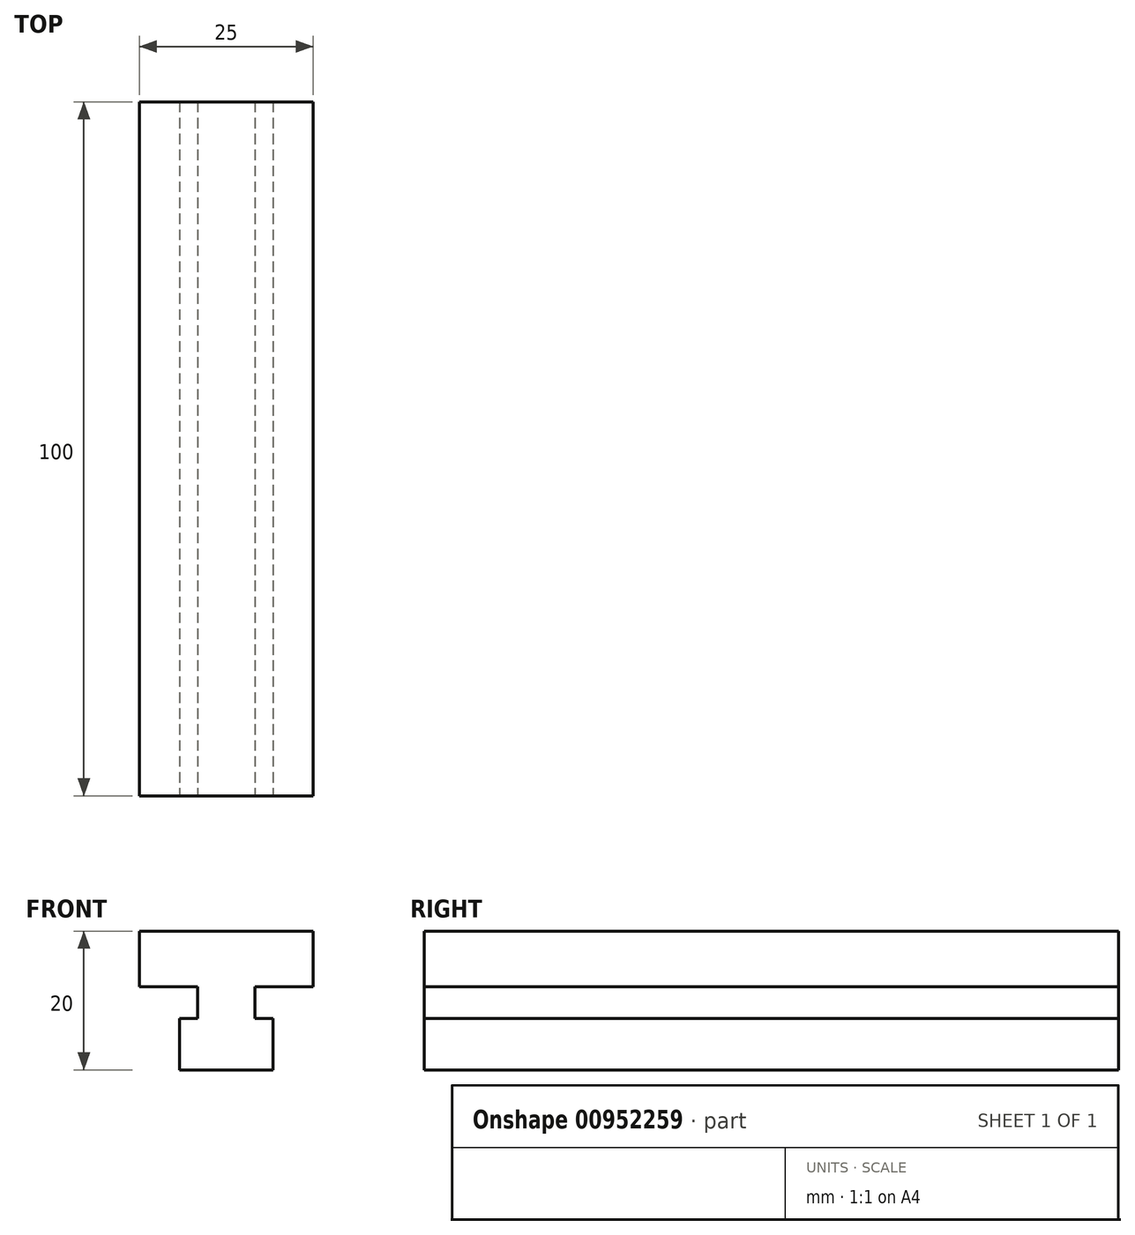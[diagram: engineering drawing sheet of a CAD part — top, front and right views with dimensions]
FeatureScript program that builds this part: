
annotation { "Feature Type Name" : "Feature", "Feature Type Description" : "" }
export const myFeature = defineFeature(function(context is Context, id is Id, definition is map)
    precondition{}
    {
        {
            var Q0;
            Q0=qCreatedBy(makeId("Front.planeOp"),FACE);
            var sketch = newSketch(context, id + "F0", { "sketchPlane" : qUnion([Q0])});
            skLineSegment(sketch, "E0", {"start": v(0, 0) * mm, "end": v(6.75, 0) * mm});
            skLineSegment(sketch, "E1", {"start": v(6.75, 0) * mm, "end": v(6.75, 7.4) * mm});
            skLineSegment(sketch, "E2", {"start": v(6.75, 7.4) * mm, "end": v(4.1, 7.4) * mm});
            skLineSegment(sketch, "E3", {"start": v(4.1, 7.4) * mm, "end": v(4.1, 12) * mm});
            skLineSegment(sketch, "E4", {"start": v(4.1, 12) * mm, "end": v(12.5, 12) * mm});
            skLineSegment(sketch, "E5", {"start": v(12.5, 12) * mm, "end": v(12.5, 20) * mm});
            skLineSegment(sketch, "E6", {"start": v(12.5, 20) * mm, "end": v(0, 20) * mm});
            skLineSegment(sketch, "E7.MirrorCS", {"start": v(-6.75, 0) * mm, "end": v(-6.75, 7.4) * mm});
            skLineSegment(sketch, "E8.MirrorCS", {"start": v(-4.1, 12) * mm, "end": v(-12.5, 12) * mm});
            skLineSegment(sketch, "E9.MirrorCS", {"start": v(-12.5, 20) * mm, "end": v(0, 20) * mm});
            skLineSegment(sketch, "E10.MirrorCS", {"start": v(-4.1, 7.4) * mm, "end": v(-4.1, 12) * mm});
            skLineSegment(sketch, "E11.MirrorCS", {"start": v(-6.75, 7.4) * mm, "end": v(-4.1, 7.4) * mm});
            skLineSegment(sketch, "E12.MirrorCS", {"start": v(0, 0) * mm, "end": v(-6.75, 0) * mm});
            skLineSegment(sketch, "E13.MirrorCS", {"start": v(-12.5, 12) * mm, "end": v(-12.5, 20) * mm});
            skSolve(sketch);
        }
        {
            var Q0;
            Q0 = qSketchRegion(id + "F0", true);
            extrude(context, id + "F1", {"entities" : qUnion([Q0]), "oppositeDirection" : true, "depth" : 100 * mm, "offsetDistance" : 25 * mm});
        }
    });
